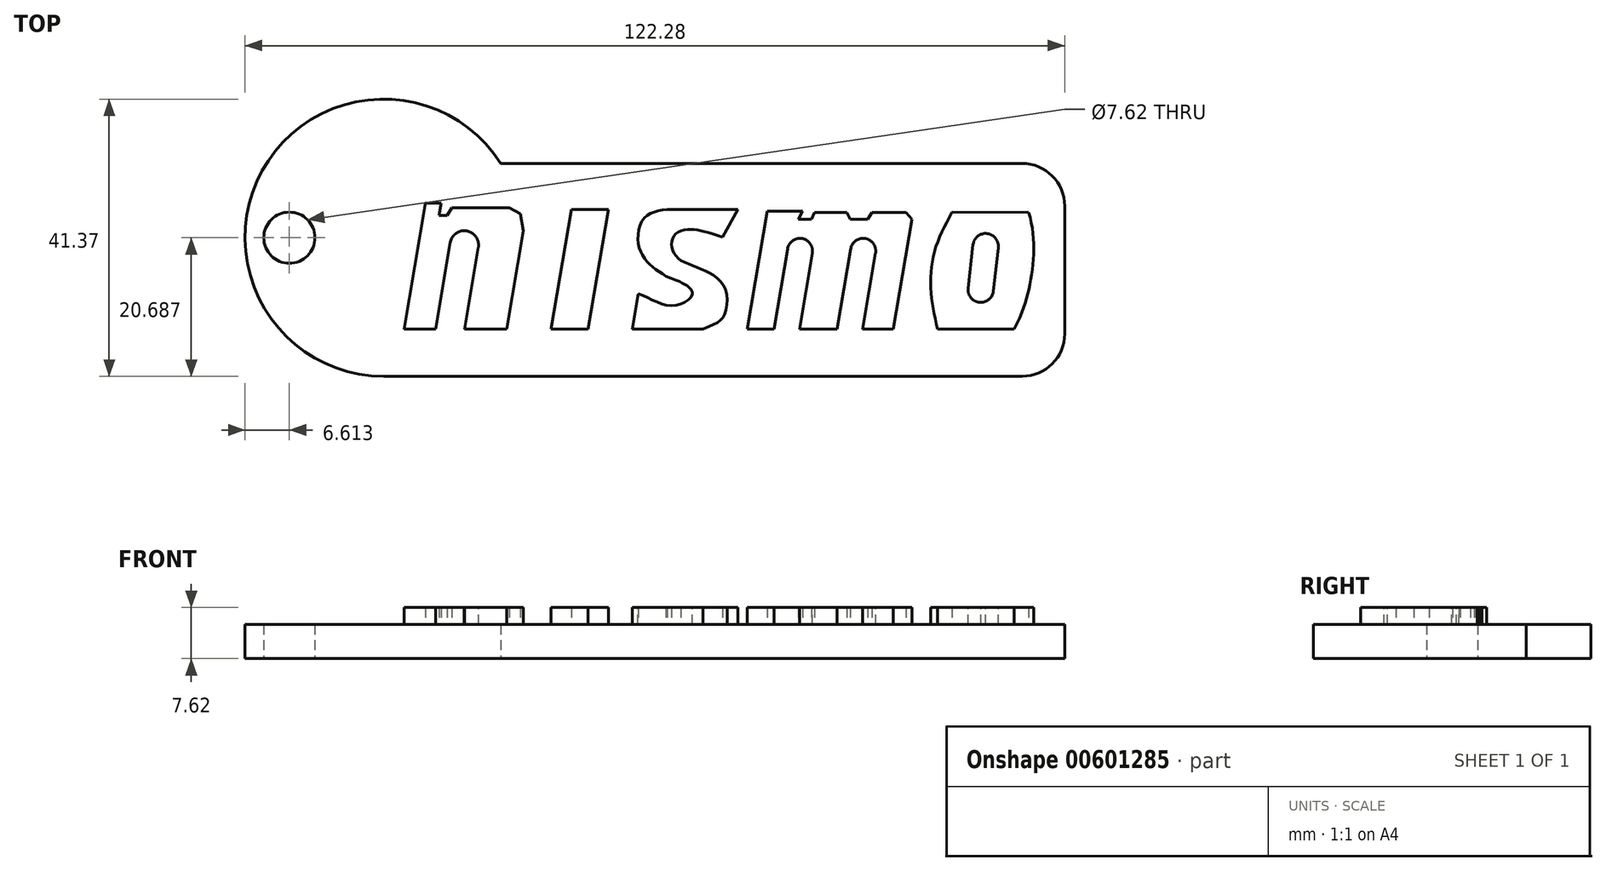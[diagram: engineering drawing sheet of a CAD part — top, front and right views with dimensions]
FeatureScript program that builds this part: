
annotation { "Feature Type Name" : "Feature", "Feature Type Description" : "" }
export const myFeature = defineFeature(function(context is Context, id is Id, definition is map)
    precondition{}
    {
        {
            var Q0;
            Q0=qCreatedBy(makeId("Top.planeOp"),FACE);
            var sketch = newSketch(context, id + "F0", { "sketchPlane" : qUnion([Q0])});
            skLineSegment(sketch, "E0.bottom", {"start": v(44.45, -15.87) * mm, "end": v(-50.8, -15.88) * mm});
            skLineSegment(sketch, "E0.top", {"start": v(44.45, 15.88) * mm, "end": v(-50.8, 15.87) * mm});
            skLineSegment(sketch, "E0.left", {"start": v(50.8, -9.52) * mm, "end": v(50.8, 9.53) * mm});
            skLineSegment(sketch, "E0.right", {"start": v(-50.8, -15.88) * mm, "end": v(-50.8, 15.88) * mm});
            skPoint(sketch, "E0.middle", {"position": v(0, 0) * mm});
            skPoint(sketch, "E1.visualSharp", {"position": v(50.8, 15.88) * mm});
            skArc(sketch, "E1.filletArc", {"start": v(50.8, 9.53) * mm, "mid": v(48.94, 14.02) * mm, "end": v(44.45, 15.88) * mm});
            skPoint(sketch, "E2.visualSharp", {"position": v(50.8, -15.87) * mm});
            skArc(sketch, "E2.filletArc", {"start": v(44.45, -15.88) * mm, "mid": v(48.94, -14.02) * mm, "end": v(50.8, -9.52) * mm});
            skCircle(sketch, "E3", {"center": v(-64.87, 4.8) * mm, "radius": 3.81 * mm});
            skArc(sketch, "E4", {"start": v(-33.33, 15.88) * mm, "mid": v(-68.92, 14.78) * mm, "end": v(-50.8, -15.88) * mm});
            skSolve(sketch);
        }
        {
            var Q0;
            {var subQ0=sQuery(id+"F0.wireOp",EDGE,"E0.right");Q0=makeQuery(id+"F0.imprint","IMPRINT",FACE,{"disambiguationData":[TD([[makeQuery(id+"F0.imprint","IMPRINT",EDGE,{"derivedFrom":subQ0}),1.0]])]});}
            var Q1;
            Q1=makeQuery(id+"F0.imprint","IMPRINT",FACE,{"disambiguationData":[TD([[makeQuery(id+"F0.imprint","IMPRINT",EDGE,{"derivedFrom":sQuery(id+"F0.wireOp",EDGE,"E0.bottom")}),-1.0]])]});
            extrude(context, id + "F1", {"entities" : qUnion([Q0, Q1]), "depth" : 5.08 * mm, "offsetDistance" : 25.4 * mm});
        }
        {
            var Q0;
            Q0=qCreatedBy(makeId("Top.planeOp"),FACE);
            var sketch = newSketch(context, id + "F2", { "sketchPlane" : qUnion([Q0])});
            skLineSegment(sketch, "E5", {"start": v(-45.24, 5.85) * mm, "end": v(-47.72, -8.84) * mm});
            skLineSegment(sketch, "E6", {"start": v(-47.72, -8.84) * mm, "end": v(-43.05, -8.84) * mm});
            skLineSegment(sketch, "E7", {"start": v(-43.05, -8.84) * mm, "end": v(-40.56, 5.85) * mm});
            skLineSegment(sketch, "E8", {"start": v(-40.56, 5.85) * mm, "end": v(-36.25, 5.85) * mm});
            skLineSegment(sketch, "E9", {"start": v(-36.25, 5.85) * mm, "end": v(-38.73, -8.84) * mm});
            skLineSegment(sketch, "E10", {"start": v(-38.73, -8.84) * mm, "end": v(-32.44, -8.84) * mm});
            skLineSegment(sketch, "E11", {"start": v(-32.44, -8.84) * mm, "end": v(-29.95, 5.85) * mm});
            skLineSegment(sketch, "E12", {"start": v(-32.05, 9.29) * mm, "end": v(-39.95, 9.29) * mm});
            skLineSegment(sketch, "E13", {"start": v(-25.83, -8.84) * mm, "end": v(-22.81, 9.03) * mm});
            skLineSegment(sketch, "E14", {"start": v(-22.81, 9.03) * mm, "end": v(-17.29, 9.03) * mm});
            skLineSegment(sketch, "E15", {"start": v(-17.29, 9.03) * mm, "end": v(-20.3, -8.84) * mm});
            skLineSegment(sketch, "E16", {"start": v(-20.3, -8.84) * mm, "end": v(-25.83, -8.84) * mm});
            skLineSegment(sketch, "E17", {"start": v(-13.7, -8.84) * mm, "end": v(-3.16, -8.84) * mm});
            skLineSegment(sketch, "E18", {"start": v(-13.7, -8.84) * mm, "end": v(-12.8, -3.55) * mm});
            skFitSpline(sketch, "E19", {"points": [v(-12.8, -3.55) * mm, v(-7.52, -5.31) * mm, v(-4.73, -3.55) * mm, v(-5.6, -2.35) * mm, v(-8.67, -0.93) * mm], "startDerivative": vector(15.32, -5.9) * mm, "endDerivative": vector(-21.25, 8.12) * mm});
            skFitSpline(sketch, "E20", {"points": [v(-3.16, -8.84) * mm, v(0, -6.8) * mm, v(0, -2.48) * mm, v(-3.16, 0) * mm, v(-6.48, 1.42) * mm], "startDerivative": vector(21.94, 9.39) * mm, "endDerivative": vector(-14.28, 7.14) * mm});
            skLineSegment(sketch, "E21", {"start": v(-8.52, 9.03) * mm, "end": v(2.02, 9.03) * mm});
            skFitSpline(sketch, "E22", {"points": [v(-8.67, -0.93) * mm, v(-11.36, 1.1) * mm, v(-12.8, 3.99) * mm, v(-11.85, 7.83) * mm, v(-8.52, 9.03) * mm], "startDerivative": vector(-11.85, 7.6) * mm, "endDerivative": vector(15.2, 2.1) * mm});
            skFitSpline(sketch, "E23", {"points": [v(-6.48, 1.42) * mm, v(-7.84, 3.5) * mm, v(-7.08, 5.5) * mm, v(-4.6, 6) * mm, v(-0.21, 4.9) * mm], "startDerivative": vector(-8.56, 6.33) * mm, "endDerivative": vector(20.13, -6.5) * mm});
            skLineSegment(sketch, "E24", {"start": v(2.02, 9.03) * mm, "end": v(-0.21, 4.9) * mm});
            skLineSegment(sketch, "E25", {"start": v(3.44, -8.84) * mm, "end": v(6.41, 8.76) * mm});
            skLineSegment(sketch, "E26", {"start": v(6.41, 8.76) * mm, "end": v(11.68, 8.76) * mm});
            skLineSegment(sketch, "E27", {"start": v(11.68, 8.76) * mm, "end": v(11.03, 7.57) * mm});
            skLineSegment(sketch, "E28", {"start": v(11.03, 7.57) * mm, "end": v(13.03, 7.57) * mm});
            skLineSegment(sketch, "E29", {"start": v(13.03, 7.57) * mm, "end": v(13.45, 8.57) * mm});
            skLineSegment(sketch, "E30", {"start": v(13.45, 8.57) * mm, "end": v(18.3, 8.57) * mm});
            skLineSegment(sketch, "E31", {"start": v(18.3, 8.57) * mm, "end": v(18.82, 7.57) * mm});
            skLineSegment(sketch, "E32", {"start": v(18.82, 7.57) * mm, "end": v(21.44, 7.57) * mm});
            skLineSegment(sketch, "E33", {"start": v(21.44, 7.57) * mm, "end": v(22.07, 8.57) * mm});
            skLineSegment(sketch, "E34", {"start": v(22.07, 8.57) * mm, "end": v(27.12, 8.57) * mm});
            skLineSegment(sketch, "E35", {"start": v(27.12, 8.57) * mm, "end": v(28.01, 7.57) * mm});
            skLineSegment(sketch, "E36", {"start": v(28.01, 7.57) * mm, "end": v(25.24, -8.84) * mm});
            skLineSegment(sketch, "E37", {"start": v(25.24, -8.84) * mm, "end": v(20.66, -8.84) * mm});
            skLineSegment(sketch, "E38", {"start": v(20.66, -8.84) * mm, "end": v(22.95, 4.72) * mm});
            skPoint(sketch, "E38.endSnap0", {"position": v(22.95, -8.84) * mm});
            skLineSegment(sketch, "E39", {"start": v(22.95, 4.72) * mm, "end": v(19.14, 4.72) * mm});
            skLineSegment(sketch, "E40", {"start": v(19.14, 4.72) * mm, "end": v(16.85, -8.84) * mm});
            skLineSegment(sketch, "E41", {"start": v(16.85, -8.84) * mm, "end": v(11.24, -8.84) * mm});
            skLineSegment(sketch, "E42", {"start": v(11.24, -8.84) * mm, "end": v(13.53, 4.72) * mm});
            skLineSegment(sketch, "E43", {"start": v(13.53, 4.72) * mm, "end": v(9.72, 4.72) * mm});
            skLineSegment(sketch, "E44", {"start": v(9.72, 4.72) * mm, "end": v(7.43, -8.84) * mm});
            skLineSegment(sketch, "E45", {"start": v(7.43, -8.84) * mm, "end": v(3.44, -8.84) * mm});
            skLineSegment(sketch, "E46", {"start": v(36.16, -4.86) * mm, "end": v(39.97, -4.86) * mm});
            skLineSegment(sketch, "E47", {"start": v(39.97, -4.86) * mm, "end": v(41.12, 5.43) * mm});
            skLineSegment(sketch, "E48", {"start": v(41.12, 5.43) * mm, "end": v(37.31, 5.43) * mm});
            skLineSegment(sketch, "E49", {"start": v(37.31, 5.43) * mm, "end": v(36.16, -4.86) * mm});
            skLineSegment(sketch, "E50", {"start": v(31.85, -8.84) * mm, "end": v(43.28, -8.84) * mm});
            skLineSegment(sketch, "E51", {"start": v(34.01, 8.61) * mm, "end": v(45.44, 8.57) * mm});
            skFitSpline(sketch, "E52", {"points": [v(31.85, -8.84) * mm, v(30.82, -2.97) * mm, v(31.4, 2.82) * mm, v(34.01, 8.61) * mm], "startDerivative": vector(-4.48, 17.34) * mm, "endDerivative": vector(9.65, 17.26) * mm});
            skFitSpline(sketch, "E53", {"points": [v(45.44, 8.57) * mm, v(46.2, 2.52) * mm, v(45.44, -2.94) * mm, v(43.28, -8.84) * mm], "startDerivative": vector(5.1, -17.77) * mm, "endDerivative": vector(-10.73, -20.71) * mm});
            skLineSegment(sketch, "E54", {"start": v(-45.24, 5.85) * mm, "end": v(-44.54, 9.96) * mm});
            skLineSegment(sketch, "E55", {"start": v(-44.54, 9.96) * mm, "end": v(-42.22, 9.96) * mm});
            skLineSegment(sketch, "E56", {"start": v(-42.22, 9.96) * mm, "end": v(-42.53, 8.14) * mm});
            skLineSegment(sketch, "E57", {"start": v(-42.53, 8.14) * mm, "end": v(-41.34, 8.14) * mm});
            skLineSegment(sketch, "E58", {"start": v(-41.34, 8.14) * mm, "end": v(-40.63, 9.29) * mm});
            skLineSegment(sketch, "E59", {"start": v(-40.63, 9.29) * mm, "end": v(-39.95, 9.29) * mm});
            skLineSegment(sketch, "E60", {"start": v(-32.05, 9.29) * mm, "end": v(-30.38, 8.36) * mm});
            skLineSegment(sketch, "E61", {"start": v(-30.38, 8.36) * mm, "end": v(-29.95, 5.85) * mm});
            skSolve(sketch);
        }
        {
            var Q0;
            Q0 = qSketchRegion(id + "F2", true);
            extrude(context, id + "F3", {"entities" : qUnion([Q0]), "operationType" : NewBodyOperationType.ADD, "depth" : 7.62 * mm, "offsetDistance" : 25.4 * mm});
        }
        {
            var Q0;
            Q0=makeQuery(id+"F3.opExtrude","SWEPT_EDGE",EDGE,{"disambiguationData":[OSD([sQuery(id+"F2.wireOp",EDGE,"E8"),sQuery(id+"F2.wireOp",EDGE,"E9")])]});
            var Q1;
            Q1=makeQuery(id+"F3.opExtrude","SWEPT_EDGE",EDGE,{"disambiguationData":[OSD([sQuery(id+"F2.wireOp",EDGE,"E7"),sQuery(id+"F2.wireOp",EDGE,"E8")])]});
            fillet(context, id + "F4", {"entities" : qUnion([Q0, Q1]), "radius" : 2.16 * mm, "tangentPropagation" : true, "allowEdgeOverflow" : false});
        }
        {
            var Q0;
            Q0=makeQuery(id+"F3.opExtrude","SWEPT_EDGE",EDGE,{"disambiguationData":[OSD([sQuery(id+"F2.wireOp",EDGE,"E38"),sQuery(id+"F2.wireOp",EDGE,"E39")])]});
            var Q1;
            Q1=makeQuery(id+"F3.opExtrude","SWEPT_EDGE",EDGE,{"disambiguationData":[OSD([sQuery(id+"F2.wireOp",EDGE,"E42"),sQuery(id+"F2.wireOp",EDGE,"E43")])]});
            var Q2;
            Q2=makeQuery(id+"F3.opExtrude","SWEPT_EDGE",EDGE,{"disambiguationData":[OSD([sQuery(id+"F2.wireOp",EDGE,"E43"),sQuery(id+"F2.wireOp",EDGE,"E44")])]});
            var Q3;
            Q3=makeQuery(id+"F3.opExtrude","SWEPT_EDGE",EDGE,{"disambiguationData":[OSD([sQuery(id+"F2.wireOp",EDGE,"E39"),sQuery(id+"F2.wireOp",EDGE,"E40")])]});
            var Q4;
            Q4=makeQuery(id+"F3.opExtrude","SWEPT_EDGE",EDGE,{"disambiguationData":[OSD([sQuery(id+"F2.wireOp",EDGE,"E48"),sQuery(id+"F2.wireOp",EDGE,"E49")])]});
            var Q5;
            Q5=makeQuery(id+"F3.opExtrude","SWEPT_EDGE",EDGE,{"disambiguationData":[OSD([sQuery(id+"F2.wireOp",EDGE,"E47"),sQuery(id+"F2.wireOp",EDGE,"E48")])]});
            var Q6;
            Q6=makeQuery(id+"F3.opExtrude","SWEPT_EDGE",EDGE,{"disambiguationData":[OSD([sQuery(id+"F2.wireOp",EDGE,"E46"),sQuery(id+"F2.wireOp",EDGE,"E49")])]});
            var Q7;
            Q7=makeQuery(id+"F3.opExtrude","SWEPT_EDGE",EDGE,{"disambiguationData":[OSD([sQuery(id+"F2.wireOp",EDGE,"E46"),sQuery(id+"F2.wireOp",EDGE,"E47")])]});
            fillet(context, id + "F5", {"entities" : qUnion([Q0, Q1, Q2, Q3, Q4, Q5, Q6, Q7]), "radius" : 1.9 * mm, "tangentPropagation" : true, "allowEdgeOverflow" : false});
        }
    });
